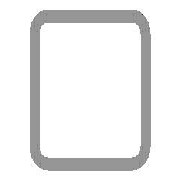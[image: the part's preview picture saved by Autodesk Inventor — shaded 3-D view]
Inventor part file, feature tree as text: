
AUTODESK INVENTOR PART (.ipt)
format: ipt  version: 2025.1 (Build 291241020, 241B)  size: 133,120 bytes
history: native  units: mm (DEFAULTED — no unit token found)
features: other x3, sketch x1, plane x1
ambient origin geometry x8: Origin, YZ Plane, XZ Plane, XY Plane, X Axis, Y Axis, Z Axis, Center Point
bodies: Solid1 (feature_tree), Body (feature_tree)
feature tree (5):
  other  "Driven Length"
  other  "Start plane"
  other  "End plane"
  sketch  "Sketch3"  dims[d3=1900.0mm d4=0.0mm d7=4.5mm d10=50.0mm d11=50.0mm d12=3.0mm d13=-0.0mm d14=1900.0mm d15=25.0mm d16=25.0mm d17=90.0deg d18=1900.0mm]
  plane  "Work Plane3"
